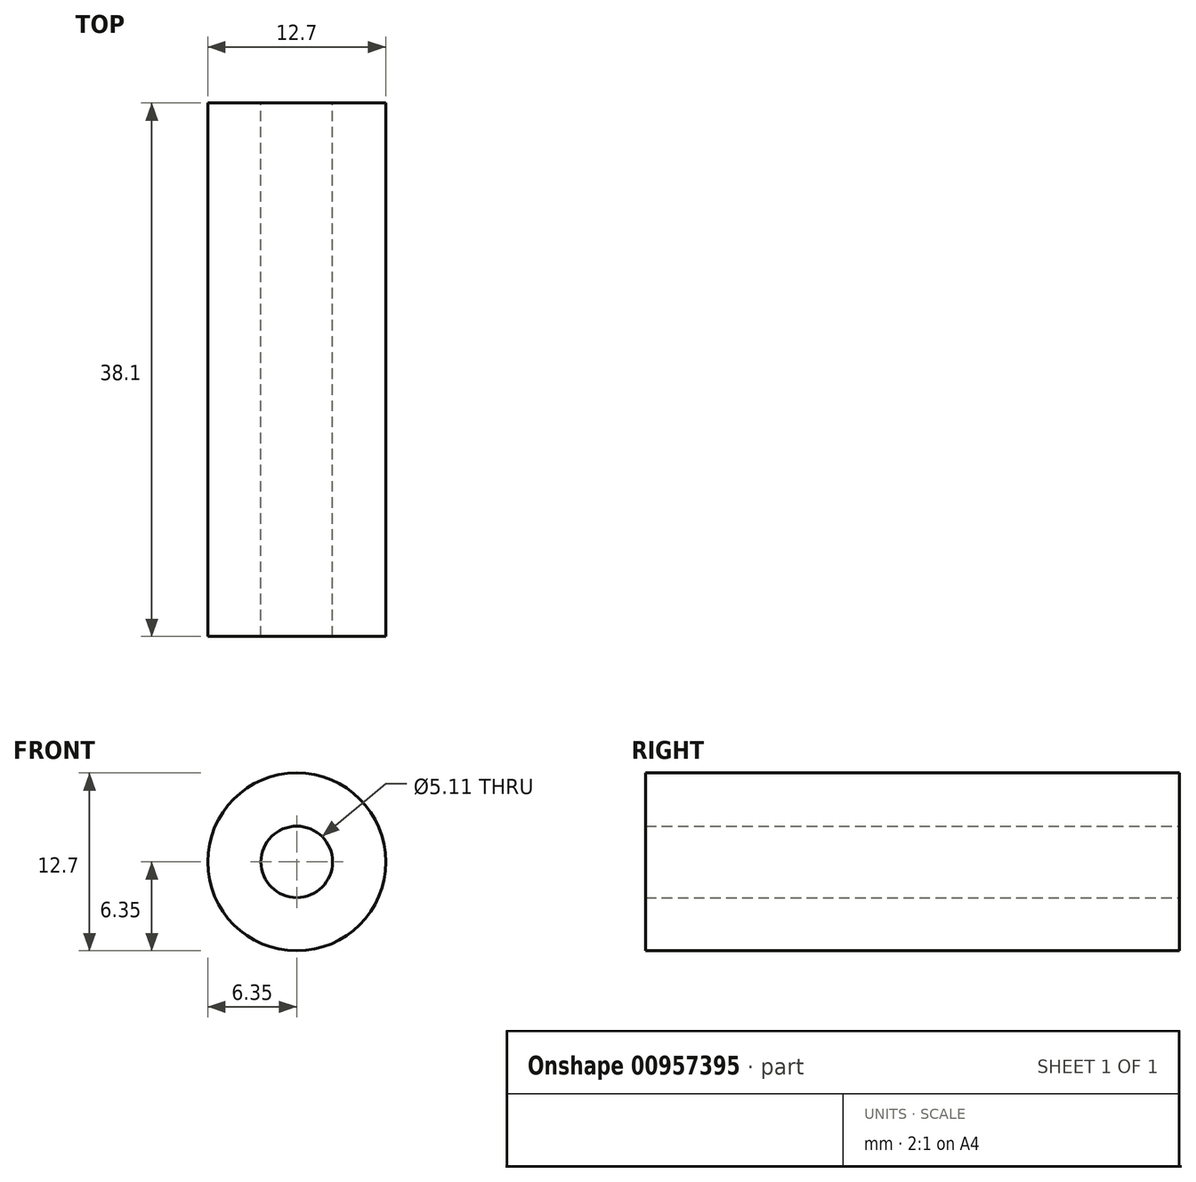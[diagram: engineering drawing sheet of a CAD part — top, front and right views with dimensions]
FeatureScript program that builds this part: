
annotation { "Feature Type Name" : "Feature", "Feature Type Description" : "" }
export const myFeature = defineFeature(function(context is Context, id is Id, definition is map)
    precondition{}
    {
        {
            var Q0;
            Q0=qCreatedBy(makeId("Front.planeOp"),FACE);
            var sketch = newSketch(context, id + "F0", { "sketchPlane" : qUnion([Q0])});
            skCircle(sketch, "E0", {"center": v(0, 0) * mm, "radius": 2.55 * mm});
            skCircle(sketch, "E1", {"center": v(0, 0) * mm, "radius": 6.35 * mm});
            skSolve(sketch);
        }
        {
            var Q0;
            Q0 = qSketchRegion(id + "F0", true);
            extrude(context, id + "F1", {"entities" : qUnion([Q0]), "depth" : 38.1 * mm, "offsetDistance" : 25.4 * mm});
        }
    });
